# Revit family: Roxtec GH frames
name_source: partatom
category: Duct Accessories
revit_build: Autodesk Revit 2017 (Build: 20190508_0315(x64)
units: mm (PartAtom-declared; Revit-internal decimal feet)

## family parameters
Cut with Voids When Loaded = No
Host = Face
Part Type = Attaches To
Round Connector Dimension = Use Diameter
Shared = No

## types (8) — shared parameters
ETIM Classification = EC002600
Flange thickness = 6 mm  [stored 0.019685 ft]
Frame depth = 60 mm  [stored 0.19685 ft]
Frame material = Steel
Manufacturer = Roxtec
Sealing material = Roxylon blue
URL = https://www.roxtec.com
Version = 2.0
zero-valued in all types: Default Elevation, NominalDepth, NominalHeight

## per-type parameters (varying)
- GH type 6x1: 2x=No; 3x=No; 4x=No; Flange h=350 mm  [stored 1.14829 ft]; Flange w=253 mm  [stored 0.830052 ft]; ID AISI316=5GH0000008261; ID AISI316 BG=122511; ID FL100 AISI316=105508; ID FL100 AISI316 BG=122264; ID FL100 GALV=122158; ID FL100 GALV BG=122388; ID GALV=5GH0000007882; ID GALV BG=109604; Title AISI316=GH 6x1 AISI316; Title AISI316 BG=GH BG 6x1 AISI316; Title FL100 AISI316=GH 6x1 FL100 AISI316; Title FL100 AISI316 BG=GH BG 6x1 FL100 AISI316; Title FL100 GALV=GH 6x1 FL100 GALV; Title FL100 GALV BG=GH BG 6x1 FL100 GALV; Title GALV=GH 6x1 GALV; Title GALV BG=GH BG 6x1 GALV; Weight AISI316=4.8; Weight AISI316 BG=5; Weight FL100 AISI316=7.4; Weight FL100 AISI316 BG=7.6; Weight FL100 GALV=7.2; Weight FL100 GALV BG=7.4; Weight GALV=4.7; Weight GALV BG=4.9; Width of cable shelf=150 mm  [stored 0.492126 ft]
- GH type 6x2: 2x=Yes; 3x=No; 4x=No; Flange h=350 mm  [stored 1.14829 ft]; Flange w=383 mm  [stored 1.25656 ft]; ID AISI316=5GH0000008179; ID AISI316 BG=122512; ID FL100 AISI316=120984; ID FL100 AISI316 BG=122265; ID FL100 GALV=122159; ID FL100 GALV BG=122389; ID GALV=5GH0000007828; ID GALV BG=110003; Title AISI316=GH 6x2 AISI316; Title AISI316 BG=GH BG 6x2 AISI316; Title FL100 AISI316=GH 6x2 FL100 AISI316; Title FL100 AISI316 BG=GH BG 6x2 FL100 AISI316; Title FL100 GALV=GH 6x2 FL100 GALV; Title FL100 GALV BG=GH BG 6x2 FL100 GALV; Title GALV=GH 6x2 GALV; Title GALV BG=GH BG 6x2 GALV; Weight AISI316=7.3; Weight AISI316 BG=7.7; Weight FL100 AISI316=10.4; Weight FL100 AISI316 BG=10.8; Weight FL100 GALV=10.2; Weight FL100 GALV BG=10.6; Weight GALV=7.2; Weight GALV BG=7.6; Width of cable shelf=300 mm
- GH type 6x3: 2x=No; 3x=Yes; 4x=No; Flange h=350 mm  [stored 1.14829 ft]; Flange w=514 mm  [stored 1.68635 ft]; ID AISI316=5GH0000009292; ID AISI316 BG=110477; ID FL100 AISI316=105509; ID FL100 AISI316 BG=122266; ID FL100 GALV=122160; ID FL100 GALV BG=122390; ID GALV=5GH0000008108; ID GALV BG=110015; Title AISI316=GH 6x3 AISI316
GH 6x3 AISI316; Title AISI316 BG=GH BG 6x3 AISI316; Title FL100 AISI316=GH 6x3 FL100 AISI316; Title FL100 AISI316 BG=GH BG 6x3 FL100 AISI316; Title FL100 GALV=GH 6x3 FL100 GALV; Title FL100 GALV BG=GH BG 6x3 FL100 GALV; Title GALV=GH 6x3 GALV; Title GALV BG=GH BG 6x3 GALV; Weight AISI316=9.8; Weight AISI316 BG=10.2; Weight FL100 AISI316=13.5; Weight FL100 AISI316 BG=13.8; Weight FL100 GALV=13.2; Weight FL100 GALV BG=13.6; Weight GALV=9.7; Weight GALV BG=10; Width of cable shelf=400 mm  [stored 1.31234 ft]
- GH type 6x4: 2x=Yes; 3x=No; 4x=Yes; Flange h=350 mm  [stored 1.14829 ft]; Flange w=644 mm  [stored 2.11286 ft]; ID AISI316=5GH0000007904; ID AISI316 BG=122513; ID FL100 AISI316=120986; ID FL100 AISI316 BG=122267; ID FL100 GALV=122161; ID FL100 GALV BG=122391; ID GALV=5GH0000008086; ID GALV BG=122626; Title AISI316=GH 6x4 AISI316; Title AISI316 BG=GH BG 6x4 AISI316; Title FL100 AISI316=GH 6x4 FL100 AISI316; Title FL100 AISI316 BG=GH BG 6x4 FL100 AISI316; Title FL100 GALV=GH 6x4 FL100 GALV; Title FL100 GALV BG=GH BG 6x4 FL100 GALV; Title GALV=GH 6x4 GALV; Title GALV BG=GH BG 6x4 GALV; Weight AISI316=12.4; Weight AISI316 BG=12.8; Weight FL100 AISI316=16.5; Weight FL100 AISI316 BG=16.9; Weight FL100 GALV=16.2; Weight FL100 GALV BG=16.6; Weight GALV=12.2; Weight GALV BG=12.5; Width of cable shelf=500 mm  [stored 1.64042 ft]
- GH type 8x1: 2x=No; 3x=No; 4x=No; Flange h=410 mm  [stored 1.34514 ft]; Flange w=253 mm  [stored 0.830052 ft]; ID AISI316=5GH0000008395; ID AISI316 BG=122538; ID FL100 AISI316=110012; ID FL100 AISI316 BG=122295; ID FL100 GALV=122181; ID FL100 GALV BG=122419; ID GALV=GH08000002115; ID GALV BG=121224; Title AISI316=GH 8x1 AISI316; Title AISI316 BG=GH BG 8x1 AISI316; Title FL100 AISI316=GH 8x1 FL100 AISI316; Title FL100 AISI316 BG=GH BG 8x1 FL100 AISI316; Title FL100 GALV=GH 8x1 FL100 GALV; Title FL100 GALV BG=GH BG 8x1 FL100 GALV; Title GALV=GH 8x1 GALV; Title GALV BG=GH BG 8x1 GALV; Weight AISI316=5.5; Weight AISI316 BG=5.6; Weight FL100 AISI316=8.3; Weight FL100 AISI316 BG=8.5; Weight FL100 GALV=8.1; Weight FL100 GALV BG=8.3; Weight GALV=5.3; Weight GALV BG=5.5; Width of cable shelf=150 mm  [stored 0.492126 ft]
- GH type 8x2: 2x=Yes; 3x=No; 4x=No; Flange h=410 mm  [stored 1.34514 ft]; Flange w=383 mm  [stored 1.25656 ft]; ID AISI316=5GH0000008124; ID AISI316 BG=122539; ID FL100 AISI316=117284; ID FL100 AISI316 BG=122296; ID FL100 GALV=117391; ID FL100 GALV BG=122420; ID GALV=5GH0000008907; ID GALV BG=116088; Title AISI316=GH 8x2 AISI316; Title AISI316 BG=GH BG 8x2 AISI316; Title FL100 AISI316=GH 8x2 FL100 AISI316; Title FL100 AISI316 BG=GH BG 8x2 FL100 AISI316; Title FL100 GALV=GH 8x2 FL100 GALV; Title FL100 GALV BG=GH BG 8x2 FL100 GALV; Title GALV=GH 8x2 GALV; Title GALV BG=GH BG 8x2 GALV; Weight AISI316=8.3; Weight AISI316 BG=8.7; Weight FL100 AISI316=11.6; Weight FL100 AISI316 BG=12; Weight FL100 GALV=11.4; Weight FL100 GALV BG=11.8; Weight GALV=8.1; Weight GALV BG=8.5; Width of cable shelf=300 mm
- GH type 8x3: 2x=No; 3x=Yes; 4x=No; Flange h=410 mm  [stored 1.34514 ft]; Flange w=514 mm  [stored 1.68635 ft]; ID AISI316=5GH0000009294; ID AISI316 BG=122540; ID FL100 AISI316=116626; ID FL100 AISI316 BG=122297; ID FL100 GALV=122182; ID FL100 GALV BG=118374; ID GALV=5GH0000008470; ID GALV BG=110838; Title AISI316=GH 8x3 AISI316; Title AISI316 BG=GH BG 8x3 AISI316; Title FL100 AISI316=GH 8x3 FL100 AISI316; Title FL100 AISI316 BG=GH BG 8x3 FL100 AISI316; Title FL100 GALV=GH 8x3 FL100 GALV; Title FL100 GALV BG=GH BG 8x3 FL100 GALV; Title GALV=GH 8x3 GALV; Title GALV BG=GH BG 8x3 GALV; Weight AISI316=11.1; Weight AISI316 BG=11.5; Weight FL100 AISI316=15; Weight FL100 AISI316 BG=15.3; Weight FL100 GALV=14.7; Weight FL100 GALV BG=15; Weight GALV=10.9; Weight GALV BG=11.3; Width of cable shelf=400 mm  [stored 1.31234 ft]
- GH type 8x4: 2x=Yes; 3x=No; 4x=Yes; Flange h=410 mm  [stored 1.34514 ft]; Flange w=644 mm  [stored 2.11286 ft]; ID AISI316=5GH0000008380; ID AISI316 BG=122541; ID FL100 AISI316=117225; ID FL100 AISI316 BG=122298; ID FL100 GALV=105207; ID FL100 GALV BG=122422; ID GALV=5GH0000008107; ID GALV BG=111344; Title AISI316=GH 8x4 AISI316
GH 8x4 AISI316; Title AISI316 BG=GH BG 8x4 AISI316; Title FL100 AISI316=GH 8x4 FL100 AISI316; Title FL100 AISI316 BG=GH BG 8x4 FL100 AISI316; Title FL100 GALV=GH 8x4 FL100 GALV; Title FL100 GALV BG=GH BG 8x4 FL100 GALV; Title GALV=GH 8x4 GALV; Title GALV BG=GH BG 8x4 GALV; Weight AISI316=13.9; Weight AISI316 BG=14.3; Weight FL100 AISI316=18.3; Weight FL100 AISI316 BG=18.7; Weight FL100 GALV=17.9; Weight FL100 GALV BG=18.3; Weight GALV=13.7; Weight GALV BG=14.1; Width of cable shelf=500 mm  [stored 1.64042 ft]

note: [stored X ft] marks values corroborated as IEEE doubles in the binary element streams (Revit-internal decimal feet)

## geometry (parser evidence)
native form markers: Sweep x4
no freeform markers — native parametric forms only
